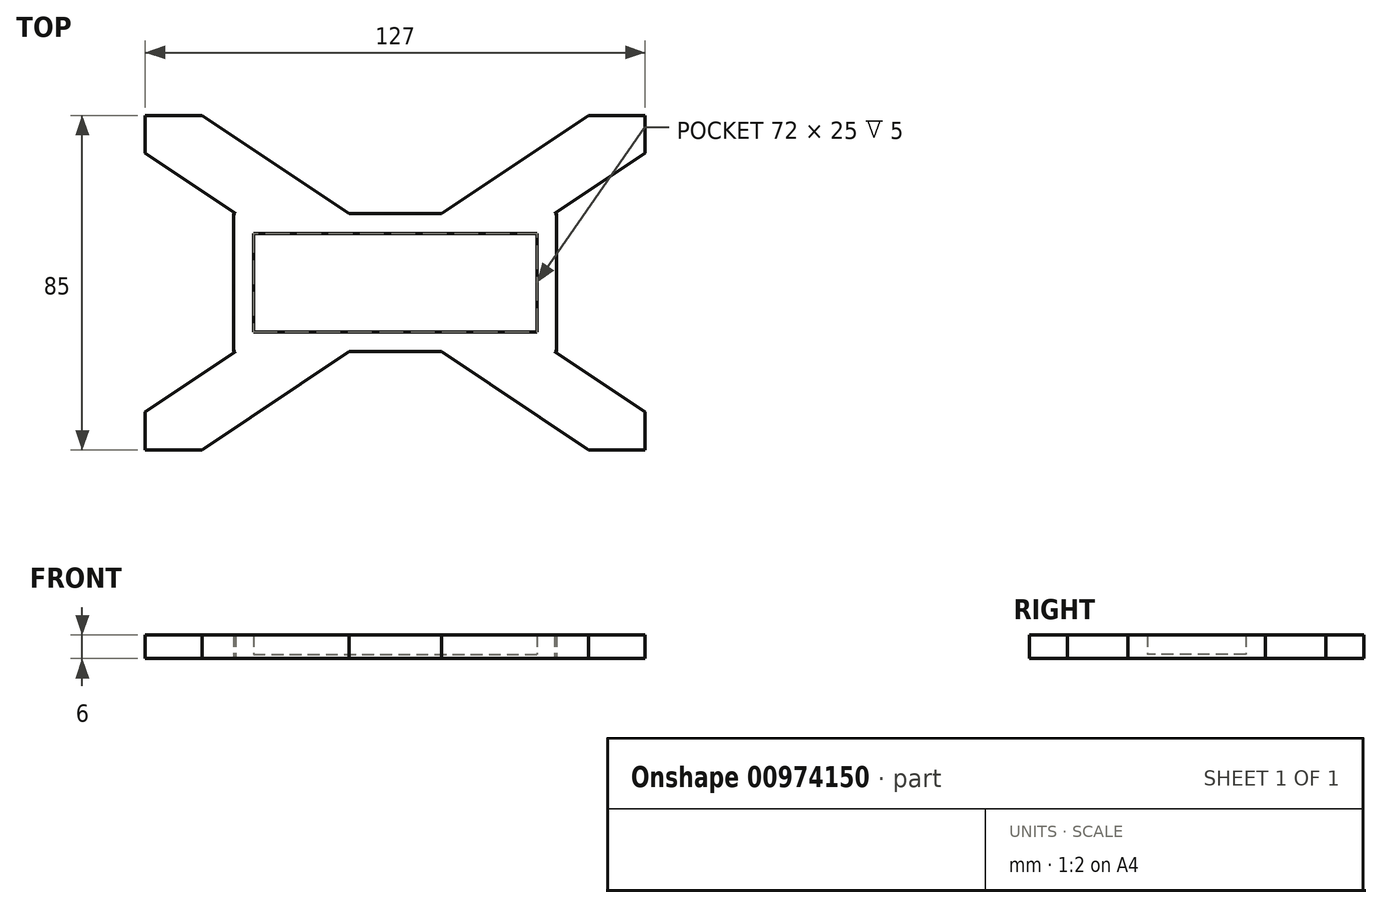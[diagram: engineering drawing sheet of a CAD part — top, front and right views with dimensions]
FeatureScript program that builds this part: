
annotation { "Feature Type Name" : "Feature", "Feature Type Description" : "" }
export const myFeature = defineFeature(function(context is Context, id is Id, definition is map)
    precondition{}
    {
        {
            var Q0;
            Q0=qCreatedBy(makeId("Top.planeOp"),FACE);
            var sketch = newSketch(context, id + "F0", { "sketchPlane" : qUnion([Q0])});
            skLineSegment(sketch, "E0.bottom", {"start": v(-63.5, 42.5) * mm, "end": v(63.5, 42.5) * mm});
            skLineSegment(sketch, "E0.top", {"start": v(-63.5, -42.5) * mm, "end": v(63.5, -42.5) * mm});
            skLineSegment(sketch, "E0.left", {"start": v(-63.5, 42.5) * mm, "end": v(-63.5, -42.5) * mm});
            skLineSegment(sketch, "E0.right", {"start": v(63.5, 42.5) * mm, "end": v(63.5, -42.5) * mm});
            skPoint(sketch, "E0.middle", {"position": v(0, 0) * mm});
            skLineSegment(sketch, "E1.bottom", {"start": v(-36, 12.5) * mm, "end": v(36, 12.5) * mm});
            skLineSegment(sketch, "E1.top", {"start": v(-36, -12.5) * mm, "end": v(36, -12.5) * mm});
            skLineSegment(sketch, "E1.left", {"start": v(-36, 12.5) * mm, "end": v(-36, -12.5) * mm});
            skLineSegment(sketch, "E1.right", {"start": v(36, 12.5) * mm, "end": v(36, -12.5) * mm});
            skLineSegment(sketch, "E2.0", {"start": v(59.05, 49.15) * mm, "end": v(11.76, 17.5) * mm});
            skLineSegment(sketch, "E3.0", {"start": v(67.95, 35.85) * mm, "end": v(40.53, 17.5) * mm});
            skLineSegment(sketch, "E4.0", {"start": v(-67.95, 35.85) * mm, "end": v(-40.53, 17.5) * mm});
            skLineSegment(sketch, "E5.0", {"start": v(-59.05, 49.15) * mm, "end": v(-11.76, 17.5) * mm});
            skLineSegment(sketch, "E6.bottom", {"start": v(-41, -17.5) * mm, "end": v(-40.53, -17.5) * mm});
            skLineSegment(sketch, "E6.top", {"start": v(-41, 17.5) * mm, "end": v(-40.53, 17.5) * mm});
            skLineSegment(sketch, "E6.left", {"start": v(-41, -17.5) * mm, "end": v(-41, 17.5) * mm});
            skLineSegment(sketch, "E6.right", {"start": v(41, -17.5) * mm, "end": v(41, 17.5) * mm});
            skLineSegment(sketch, "E7.trimOffspring", {"start": v(-11.76, 17.5) * mm, "end": v(11.76, 17.5) * mm});
            skLineSegment(sketch, "E8.trimOffspring", {"start": v(40.53, 17.5) * mm, "end": v(41, 17.5) * mm});
            skLineSegment(sketch, "E9.trimOffspring", {"start": v(40.53, -17.5) * mm, "end": v(67.95, -35.85) * mm});
            skLineSegment(sketch, "E10.trimOffspring", {"start": v(40.53, -17.5) * mm, "end": v(41, -17.5) * mm});
            skLineSegment(sketch, "E11.trimOffspring", {"start": v(-11.76, -17.5) * mm, "end": v(11.76, -17.5) * mm});
            skLineSegment(sketch, "E12.trimOffspring", {"start": v(-40.53, -17.5) * mm, "end": v(-67.95, -35.85) * mm});
            skLineSegment(sketch, "E13.trimOffspring", {"start": v(-11.76, -17.5) * mm, "end": v(-59.05, -49.15) * mm});
            skLineSegment(sketch, "E14.trimOffspring", {"start": v(11.76, -17.5) * mm, "end": v(59.05, -49.15) * mm});
            skSolve(sketch);
        }
        {
            var Q0;
            Q0=makeQuery(id+"F0.imprint","IMPRINT",FACE,{"disambiguationData":[TD([[makeQuery(id+"F0.imprint","IMPRINT",EDGE,{"derivedFrom":sQuery(id+"F0.wireOp",EDGE,"E1.bottom")}),1.0]])]});
            extrude(context, id + "F1", {"entities" : qUnion([Q0]), "depth" : 6 * mm, "offsetDistance" : 25 * mm});
        }
        {
            var Q0;
            Q0=makeQuery(id+"F0.imprint","IMPRINT",FACE,{"disambiguationData":[TD([[makeQuery(id+"F0.imprint","IMPRINT",EDGE,{"derivedFrom":sQuery(id+"F0.wireOp",EDGE,"E1.bottom")}),-1.0]])]});
            extrude(context, id + "F2", {"entities" : qUnion([Q0]), "operationType" : NewBodyOperationType.ADD, "depth" : 1 * mm, "offsetDistance" : 25 * mm});
        }
    });
